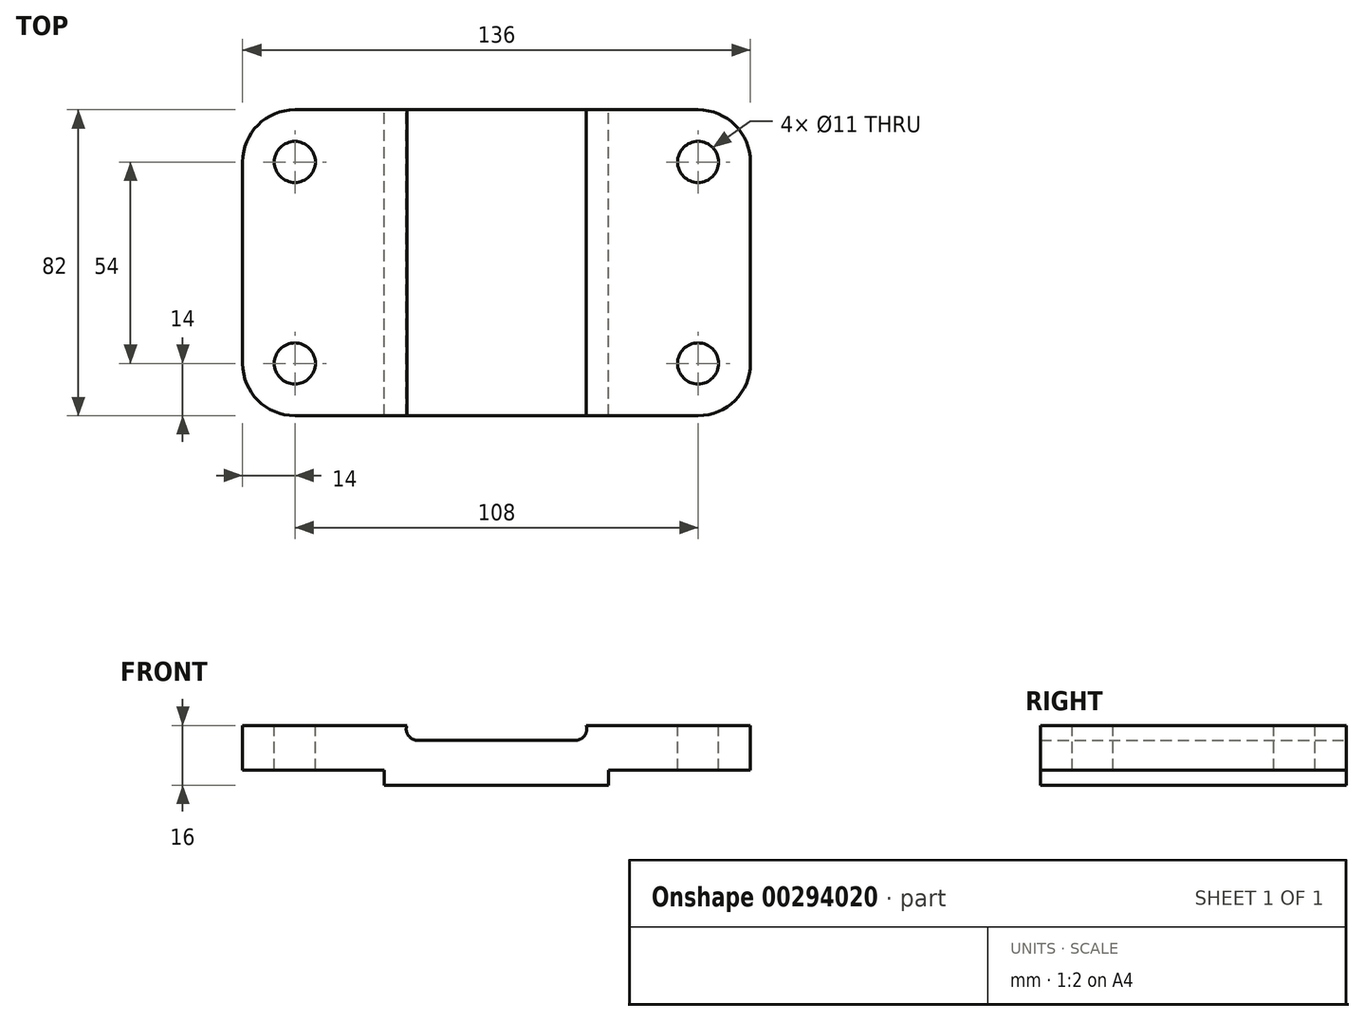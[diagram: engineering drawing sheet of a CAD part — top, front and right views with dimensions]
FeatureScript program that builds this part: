
annotation { "Feature Type Name" : "Feature", "Feature Type Description" : "" }
export const myFeature = defineFeature(function(context is Context, id is Id, definition is map)
    precondition{}
    {
        {
            var Q0;
            Q0=qCreatedBy(makeId("Front.planeOp"),FACE);
            var sketch = newSketch(context, id + "F0", { "sketchPlane" : qUnion([Q0])});
            skLineSegment(sketch, "E0", {"start": v(0, 32.5) * mm, "end": v(0, -32.5) * mm, "construction": true});
            skLineSegment(sketch, "E1", {"start": v(0, 0) * mm, "end": v(21.17, 0) * mm});
            skLineSegment(sketch, "E2", {"start": v(24, 4) * mm, "end": v(68, 4) * mm});
            skLineSegment(sketch, "E3", {"start": v(68, 4) * mm, "end": v(68, -8) * mm});
            skLineSegment(sketch, "E4", {"start": v(68, -8) * mm, "end": v(30, -8) * mm});
            skLineSegment(sketch, "E5", {"start": v(30, -8) * mm, "end": v(30, -12) * mm});
            skLineSegment(sketch, "E6", {"start": v(30, -12) * mm, "end": v(0, -12) * mm});
            skLineSegment(sketch, "E7.MirrorCS", {"start": v(-24, 4) * mm, "end": v(-68, 4) * mm});
            skLineSegment(sketch, "E8.MirrorCS", {"start": v(-30, -8) * mm, "end": v(-30, -12) * mm});
            skLineSegment(sketch, "E9.MirrorCS", {"start": v(-68, -8) * mm, "end": v(-30, -8) * mm});
            skLineSegment(sketch, "E10.MirrorCS", {"start": v(-68, 4) * mm, "end": v(-68, -8) * mm});
            skLineSegment(sketch, "E11.MirrorCS", {"start": v(0, 0) * mm, "end": v(-21.17, 0) * mm});
            skLineSegment(sketch, "E12.MirrorCS", {"start": v(-30, -12) * mm, "end": v(0, -12) * mm});
            skArc(sketch, "E13", {"start": v(21.17, 0) * mm, "mid": v(23.62, 1.27) * mm, "end": v(24, 4) * mm});
            skArc(sketch, "E14.MirrorCS", {"start": v(-21.17, 0) * mm, "mid": v(-23.62, 1.27) * mm, "end": v(-24, 4) * mm});
            skSolve(sketch);
        }
        {
            var Q0;
            Q0=makeQuery(id+"F0.imprint","IMPRINT",FACE,{"disambiguationData":[TD([[makeQuery(id+"F0.imprint","IMPRINT",EDGE,{"derivedFrom":sQuery(id+"F0.wireOp",EDGE,"E1")}),-1.0]])]});
            extrude(context, id + "F1", {"entities" : qUnion([Q0]), "depth" : 82 * mm});
        }
        {
            var Q0;
            Q0=makeQuery(id+"F1.opExtrude","SWEPT_FACE",FACE,{"disambiguationData":[OSD([sQuery(id+"F0.wireOp",EDGE,"E2")])]});
            var sketch = newSketch(context, id + "F2", { "sketchPlane" : qUnion([Q0])});
            skPoint(sketch, "E15.visualSharp", {"position": v(-68, 0) * mm});
            skArc(sketch, "E15.filletArc", {"start": v(-54, 0) * mm, "mid": v(-63.9, -4.1) * mm, "end": v(-68, -14) * mm});
            skLineSegment(sketch, "E16", {"start": v(0, 0) * mm, "end": v(0, -82) * mm, "construction": true});
            skLineSegment(sketch, "E17", {"start": v(68, -41) * mm, "end": v(-68, -41) * mm, "construction": true});
            skArc(sketch, "E18.MirrorCS", {"start": v(-54, -82) * mm, "mid": v(-63.9, -77.9) * mm, "end": v(-68, -68) * mm});
            skArc(sketch, "E19.MirrorCS", {"start": v(54, 0) * mm, "mid": v(63.9, -4.1) * mm, "end": v(68, -14) * mm});
            skArc(sketch, "E20.MirrorCS", {"start": v(54, -82) * mm, "mid": v(63.9, -77.9) * mm, "end": v(68, -68) * mm});
            skLineSegment(sketch, "E21", {"start": v(-68, -14) * mm, "end": v(-68, 0) * mm});
            skLineSegment(sketch, "E22", {"start": v(-54, 0) * mm, "end": v(-68, 0) * mm});
            skLineSegment(sketch, "E23", {"start": v(-68, -68) * mm, "end": v(-68, -82) * mm});
            skLineSegment(sketch, "E24", {"start": v(-68, -82) * mm, "end": v(-54, -82) * mm});
            skLineSegment(sketch, "E25", {"start": v(54, -82) * mm, "end": v(68, -82) * mm});
            skLineSegment(sketch, "E26", {"start": v(68, -82) * mm, "end": v(68, -68) * mm});
            skLineSegment(sketch, "E27", {"start": v(68, -14) * mm, "end": v(68, 0) * mm});
            skLineSegment(sketch, "E28", {"start": v(68, 0) * mm, "end": v(54, 0) * mm});
            skSolve(sketch);
        }
        {
            var Q0;
            Q0 = qSketchRegion(id + "F2", true);
            extrude(context, id + "F3", {"entities" : qUnion([Q0]), "operationType" : NewBodyOperationType.REMOVE, "oppositeDirection" : true, "depth" : 25 * mm});
        }
        {
            var Q0;
            Q0=makeQuery(id+"F1.opExtrude","SWEPT_FACE",FACE,{"disambiguationData":[OSD([sQuery(id+"F0.wireOp",EDGE,"E7.MirrorCS")])]});
            var sketch = newSketch(context, id + "F4", { "sketchPlane" : qUnion([Q0])});
            skCircle(sketch, "E29", {"center": v(-54, -14) * mm, "radius": 5.5 * mm});
            skCircle(sketch, "E30.0.1.0", {"center": v(-54, -68) * mm, "radius": 5.5 * mm});
            skCircle(sketch, "E30.1.0.0", {"center": v(54, -14) * mm, "radius": 5.5 * mm});
            skCircle(sketch, "E30.1.1.0", {"center": v(54, -68) * mm, "radius": 5.5 * mm});
            skSolve(sketch);
        }
        {
            var Q0;
            Q0 = qSketchRegion(id + "F4", true);
            extrude(context, id + "F5", {"entities" : qUnion([Q0]), "operationType" : NewBodyOperationType.REMOVE, "oppositeDirection" : true, "depth" : 25 * mm});
        }
    });
